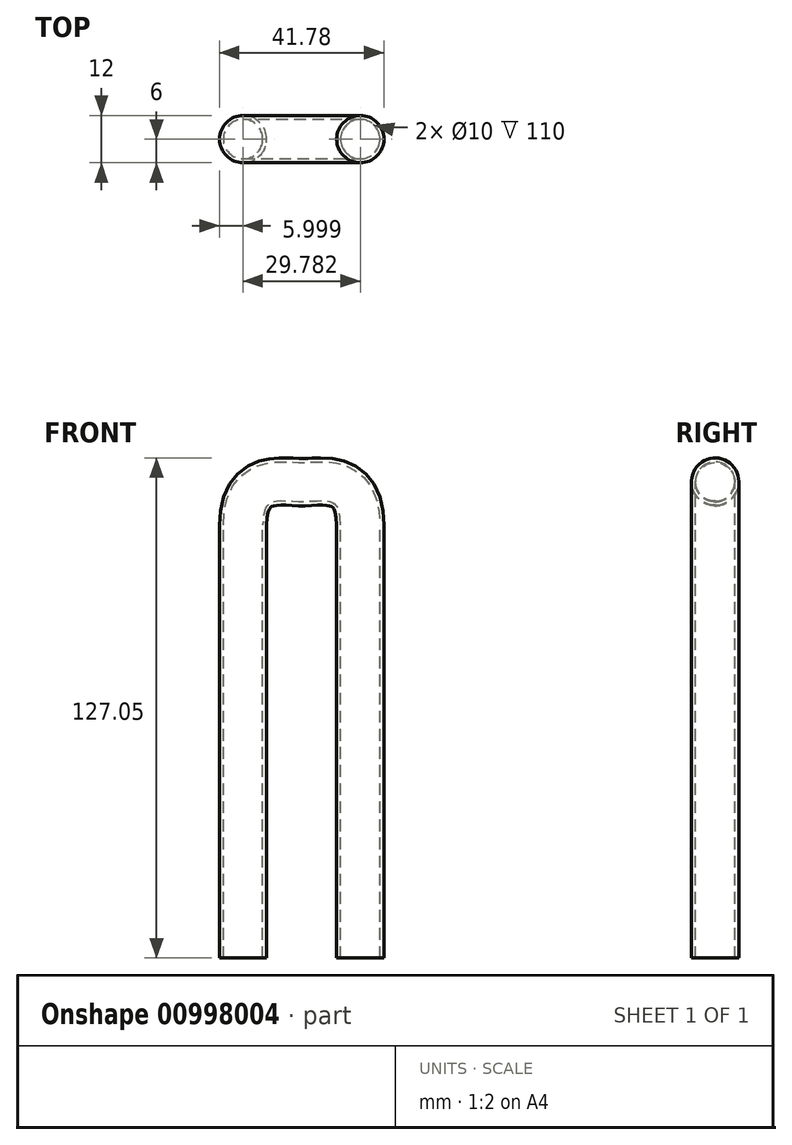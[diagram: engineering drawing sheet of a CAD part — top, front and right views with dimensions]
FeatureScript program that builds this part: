
annotation { "Feature Type Name" : "Feature", "Feature Type Description" : "" }
export const myFeature = defineFeature(function(context is Context, id is Id, definition is map)
    precondition{}
    {
        {
            var Q0;
            Q0=qCreatedBy(makeId("Front.planeOp"),FACE);
            var sketch = newSketch(context, id + "F0", { "sketchPlane" : qUnion([Q0])});
            skFitSpline(sketch, "E0", {"points": [v(-12, 0) * mm, v(0, 8) * mm, v(12, 0) * mm], "startDerivative": vector(0, 60) * mm, "endDerivative": vector(0, -60) * mm});
            skCircle(sketch, "E1", {"center": v(12, 0) * mm, "radius": 1.25 * mm});
            skSolve(sketch);
        }
        {
            var Q0;
            Q0=sQuery(id+"F0.wireOp",VERTEX,"E0.end");
            var Q1;
            Q1=sQuery(id+"F0.wireOp",EDGE,"E0");
            cPlane(context, id + "F1", {"entities" : qUnion([Q0, Q1]), "cplaneType" : CPlaneType.CURVE_POINT, "offset" : 25 * mm, "width" : 150 * mm, "height" : 150 * mm});
        }
        {
            var Q0;
            Q0=qCreatedBy(id+"F1.planeOp",FACE);
            var sketch = newSketch(context, id + "F2", { "sketchPlane" : qUnion([Q0])});
            skCircle(sketch, "E2", {"center": v(14.9, 0) * mm, "radius": 5 * mm});
            skCircle(sketch, "E3", {"center": v(14.9, 0) * mm, "radius": 6 * mm});
            skSolve(sketch);
        }
        {
            var Q0;
            Q0=makeQuery(id+"F2.imprint","IMPRINT",FACE,{"disambiguationData":[TD([[makeQuery(id+"F2.imprint","IMPRINT",EDGE,{"derivedFrom":sQuery(id+"F2.wireOp",EDGE,"E2")}),-1.0]])]});
            var Q1;
            Q1=sQuery(id+"F0.wireOp",EDGE,"E0");
            sweep(context, id + "F3", {"profiles" : qUnion([Q0]), "path" : qUnion([Q1])});
        }
        {
            var Q0;
            Q0=makeQuery(id+"F3.opSweep","CAP_FACE",FACE,{"disambiguationData":[OSD([sQuery(id+"F0.wireOp",VERTEX,"E0.start"),sQuery(id+"F2.wireOp",EDGE,"E2"),sQuery(id+"F2.wireOp",EDGE,"E3")])],"isStart":false});
            var Q1;
            Q1=makeQuery(id+"F3.opSweep","CAP_FACE",FACE,{"disambiguationData":[OSD([sQuery(id+"F0.wireOp",VERTEX,"E0.end"),sQuery(id+"F2.wireOp",EDGE,"E2"),sQuery(id+"F2.wireOp",EDGE,"E3")])],"isStart":true});
            extrude(context, id + "F4", {"entities" : qUnion([Q0, Q1]), "operationType" : NewBodyOperationType.ADD, "depth" : 110 * mm, "offsetDistance" : 25 * mm});
        }
    });
